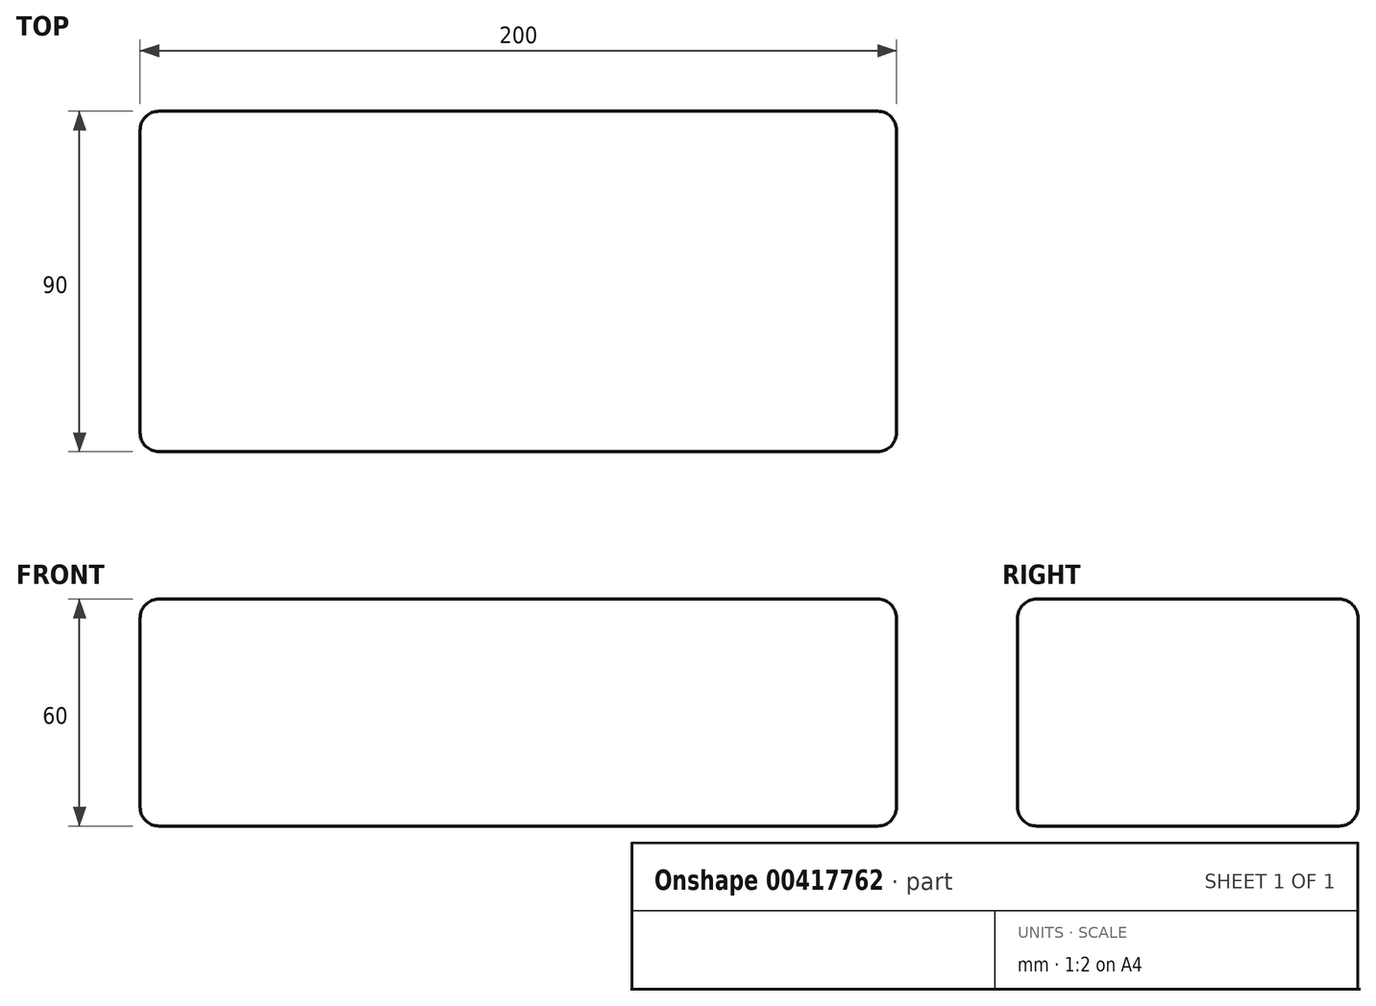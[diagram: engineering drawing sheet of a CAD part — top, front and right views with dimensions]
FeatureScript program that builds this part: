
annotation { "Feature Type Name" : "Feature", "Feature Type Description" : "" }
export const myFeature = defineFeature(function(context is Context, id is Id, definition is map)
    precondition{}
    {
        {
            var Q0;
            Q0=qCreatedBy(makeId("Top.planeOp"),FACE);
            var sketch = newSketch(context, id + "F0", { "sketchPlane" : qUnion([Q0])});
            skLineSegment(sketch, "E0.bottom", {"start": v(458.05, -221.7) * mm, "end": v(658.05, -221.7) * mm});
            skLineSegment(sketch, "E0.top", {"start": v(458.05, -311.7) * mm, "end": v(658.05, -311.7) * mm});
            skLineSegment(sketch, "E0.left", {"start": v(458.05, -221.7) * mm, "end": v(458.05, -311.7) * mm});
            skLineSegment(sketch, "E0.right", {"start": v(658.05, -221.7) * mm, "end": v(658.05, -311.7) * mm});
            skSolve(sketch);
        }
        {
            var Q0;
            Q0=makeQuery(id+"F0.imprint","IMPRINT",FACE,{"disambiguationData":[TD([[makeQuery(id+"F0.imprint","IMPRINT",EDGE,{"derivedFrom":sQuery(id+"F0.wireOp",EDGE,"E0.bottom")}),-1.0]])]});
            extrude(context, id + "F1", {"entities" : qUnion([Q0]), "depth" : 60 * mm});
        }
        {
            var Q0;
            Q0=makeQuery(id+"F1.opExtrude","SWEPT_EDGE",EDGE,{"disambiguationData":[OSD([sQuery(id+"F0.wireOp",EDGE,"E0.bottom"),sQuery(id+"F0.wireOp",EDGE,"E0.left")])]});
            var Q1;
            Q1=makeQuery(id+"F1.opExtrude","CAP_EDGE",EDGE,{"disambiguationData":[OSD([sQuery(id+"F0.wireOp",EDGE,"E0.bottom")])],"isStart":false});
            var Q2;
            Q2=makeQuery(id+"F1.opExtrude","CAP_EDGE",EDGE,{"disambiguationData":[OSD([sQuery(id+"F0.wireOp",EDGE,"E0.bottom")])],"isStart":true});
            var Q3;
            Q3=makeQuery(id+"F1.opExtrude","CAP_EDGE",EDGE,{"disambiguationData":[OSD([sQuery(id+"F0.wireOp",EDGE,"E0.left")])],"isStart":false});
            var Q4;
            Q4=makeQuery(id+"F1.opExtrude","CAP_EDGE",EDGE,{"disambiguationData":[OSD([sQuery(id+"F0.wireOp",EDGE,"E0.top")])],"isStart":false});
            var Q5;
            Q5=makeQuery(id+"F1.opExtrude","CAP_EDGE",EDGE,{"disambiguationData":[OSD([sQuery(id+"F0.wireOp",EDGE,"E0.right")])],"isStart":false});
            var Q6;
            Q6=makeQuery(id+"F1.opExtrude","CAP_EDGE",EDGE,{"disambiguationData":[OSD([sQuery(id+"F0.wireOp",EDGE,"E0.left")])],"isStart":true});
            var Q7;
            Q7=makeQuery(id+"F1.opExtrude","CAP_EDGE",EDGE,{"disambiguationData":[OSD([sQuery(id+"F0.wireOp",EDGE,"E0.top")])],"isStart":true});
            var Q8;
            Q8=makeQuery(id+"F1.opExtrude","SWEPT_EDGE",EDGE,{"disambiguationData":[OSD([sQuery(id+"F0.wireOp",EDGE,"E0.top"),sQuery(id+"F0.wireOp",EDGE,"E0.right")])]});
            var Q9;
            Q9=makeQuery(id+"F1.opExtrude","CAP_EDGE",EDGE,{"disambiguationData":[OSD([sQuery(id+"F0.wireOp",EDGE,"E0.right")])],"isStart":true});
            var Q10;
            Q10=makeQuery(id+"F1.opExtrude","SWEPT_EDGE",EDGE,{"disambiguationData":[OSD([sQuery(id+"F0.wireOp",EDGE,"E0.bottom"),sQuery(id+"F0.wireOp",EDGE,"E0.right")])]});
            var Q11;
            Q11=makeQuery(id+"F1.opExtrude","SWEPT_EDGE",EDGE,{"disambiguationData":[OSD([sQuery(id+"F0.wireOp",EDGE,"E0.top"),sQuery(id+"F0.wireOp",EDGE,"E0.left")])]});
            fillet(context, id + "F2", {"entities" : qUnion([Q0, Q1, Q2, Q3, Q4, Q5, Q6, Q7, Q8, Q9, Q10, Q11]), "radius" : 5 * mm, "tangentPropagation" : true, "allowEdgeOverflow" : false});
        }
    });
